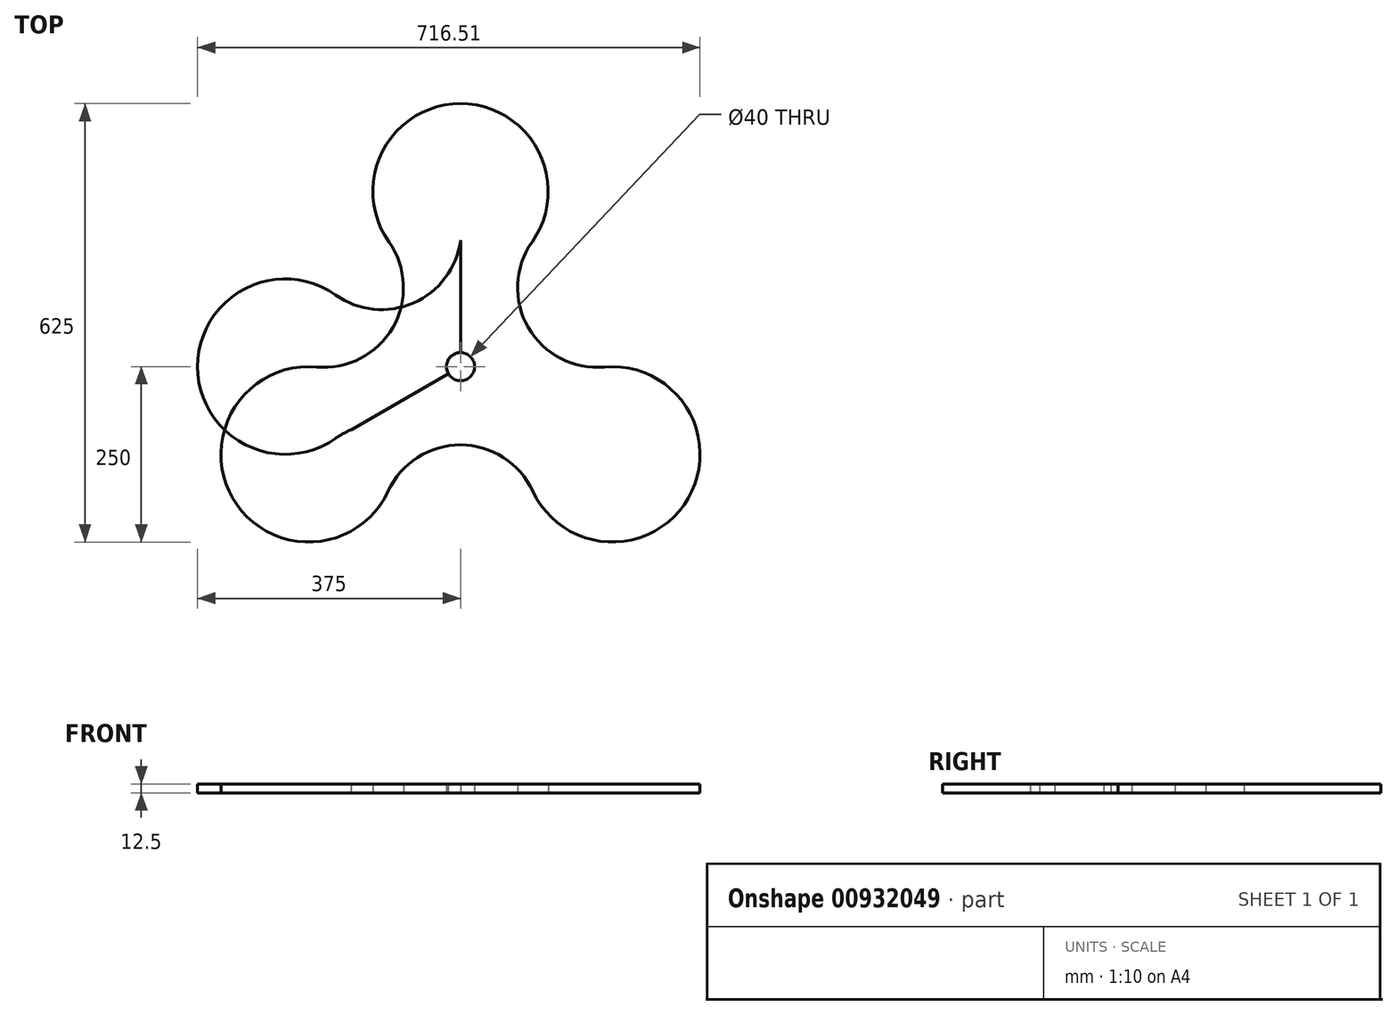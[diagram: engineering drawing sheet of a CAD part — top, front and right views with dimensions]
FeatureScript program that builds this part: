
annotation { "Feature Type Name" : "Feature", "Feature Type Description" : "" }
export const myFeature = defineFeature(function(context is Context, id is Id, definition is map)
    precondition{}
    {
        {
            var Q0;
            Q0=qCreatedBy(makeId("Top.planeOp"),FACE);
            var sketch = newSketch(context, id + "F0", { "sketchPlane" : qUnion([Q0])});
            skCircle(sketch, "E0", {"center": v(0, 0) * mm, "radius": 20 * mm});
            skCircle(sketch, "E1", {"center": v(0, 0) * mm, "radius": 65 * mm, "construction": true});
            skCircle(sketch, "E2", {"center": v(0, 0) * mm, "radius": 100 * mm});
            skLineSegment(sketch, "E3", {"start": v(0, 0) * mm, "end": v(0, 383.92) * mm, "construction": true});
            skCircle(sketch, "E4", {"center": v(0, 0) * mm, "radius": 250 * mm, "construction": true});
            skCircle(sketch, "E5", {"center": v(0, 0) * mm, "radius": 225 * mm, "construction": true});
            skLineSegment(sketch, "E6.1.0", {"start": v(0, 0) * mm, "end": v(-332.48, 191.96) * mm, "construction": true});
            skLineSegment(sketch, "E6.2.0", {"start": v(0, 0) * mm, "end": v(-332.48, -191.96) * mm, "construction": true});
            skLineSegment(sketch, "E6.3.0", {"start": v(0, 0) * mm, "end": v(0, -383.92) * mm, "construction": true});
            skLineSegment(sketch, "E6.4.0", {"start": v(0, 0) * mm, "end": v(332.48, -191.96) * mm, "construction": true});
            skLineSegment(sketch, "E6.5.0", {"start": v(0, 0) * mm, "end": v(332.48, 191.96) * mm, "construction": true});
            skArc(sketch, "E7", {"start": v(102.13, 177.93) * mm, "mid": v(0, 375) * mm, "end": v(-102.13, 177.93) * mm});
            skArc(sketch, "E8", {"start": v(102.13, 177.93) * mm, "mid": v(96.57, 55.76) * mm, "end": v(205.16, -0.52) * mm});
            skArc(sketch, "E9.1.0", {"start": v(-205.16, -0.52) * mm, "mid": v(-324.76, -187.5) * mm, "end": v(-103.03, -177.41) * mm});
            skArc(sketch, "E9.1.1", {"start": v(-205.16, -0.52) * mm, "mid": v(-96.57, 55.76) * mm, "end": v(-102.13, 177.93) * mm});
            skArc(sketch, "E9.2.0", {"start": v(103.03, -177.41) * mm, "mid": v(324.76, -187.5) * mm, "end": v(205.16, -0.52) * mm});
            skArc(sketch, "E9.2.1", {"start": v(103.03, -177.41) * mm, "mid": v(0, -111.52) * mm, "end": v(-103.03, -177.41) * mm});
            skSolve(sketch);
        }
        {
            var Q0;
            Q0=makeQuery(id+"F0.imprint","IMPRINT",FACE,{"disambiguationData":[TD([[makeQuery(id+"F0.imprint","IMPRINT",EDGE,{"derivedFrom":sQuery(id+"F0.wireOp",EDGE,"E2")}),-1.0]])]});
            var Q1;
            Q1=makeQuery(id+"F0.imprint","IMPRINT",FACE,{"disambiguationData":[TD([[makeQuery(id+"F0.imprint","IMPRINT",EDGE,{"derivedFrom":sQuery(id+"F0.wireOp",EDGE,"E0")}),-1.0]])]});
            extrude(context, id + "F1", {"entities" : qUnion([Q0, Q1]), "depth" : 12.5 * mm, "offsetDistance" : 25 * mm});
        }
        {
            var Q0;
            Q0=qCreatedBy(makeId("Top.planeOp"),FACE);
            var sketch = newSketch(context, id + "F2", { "sketchPlane" : qUnion([Q0])});
            skLineSegment(sketch, "E10", {"start": v(0, 0) * mm, "end": v(0, 416.53) * mm, "construction": true});
            skLineSegment(sketch, "E11.1.0", {"start": v(-10, 17.32) * mm, "end": v(-208.27, 360.73) * mm, "construction": true});
            skLineSegment(sketch, "E11.2.0", {"start": v(0, 0) * mm, "end": v(-360.73, 208.27) * mm, "construction": true});
            skLineSegment(sketch, "E11.3.0", {"start": v(0, 0) * mm, "end": v(-416.53, 0) * mm, "construction": true});
            skLineSegment(sketch, "E11.4.0", {"start": v(0, 0) * mm, "end": v(-360.73, -208.27) * mm, "construction": true});
            skLineSegment(sketch, "E11.5.0", {"start": v(0, 0) * mm, "end": v(-208.27, -360.73) * mm, "construction": true});
            skLineSegment(sketch, "E11.6.0", {"start": v(0, 0) * mm, "end": v(0, -416.53) * mm, "construction": true});
            skLineSegment(sketch, "E11.7.0", {"start": v(0, 0) * mm, "end": v(208.27, -360.73) * mm, "construction": true});
            skLineSegment(sketch, "E11.8.0", {"start": v(0, 0) * mm, "end": v(360.73, -208.27) * mm, "construction": true});
            skLineSegment(sketch, "E11.9.0", {"start": v(20, 0) * mm, "end": v(416.53, 0) * mm, "construction": true});
            skLineSegment(sketch, "E11.10.0", {"start": v(0, 0) * mm, "end": v(360.73, 208.27) * mm, "construction": true});
            skLineSegment(sketch, "E11.11.0", {"start": v(0, 0) * mm, "end": v(208.27, 360.73) * mm, "construction": true});
            skPoint(sketch, "E11.center", {"position": v(0, 0) * mm});
            skArc(sketch, "E12.0", {"start": v(102.13, 177.93) * mm, "mid": v(90.88, 67.03) * mm, "end": v(179.94, 0) * mm});
            skArc(sketch, "E13.0", {"start": v(-89.97, 155.83) * mm, "mid": v(-95.43, 167.22) * mm, "end": v(-102.13, 177.93) * mm});
            skLineSegment(sketch, "E14", {"start": v(-10, 17.32) * mm, "end": v(-89.97, 155.83) * mm});
            skLineSegment(sketch, "E15", {"start": v(20, 0) * mm, "end": v(179.94, 0) * mm});
            skArc(sketch, "E16.0", {"start": v(20, 0) * mm, "mid": v(10, 17.32) * mm, "end": v(-10, 17.32) * mm});
            skArc(sketch, "E17.0", {"start": v(102.13, 177.93) * mm, "mid": v(0, 375) * mm, "end": v(-102.13, 177.93) * mm});
            skArc(sketch, "E18.0.0", {"start": v(-102.13, 177.93) * mm, "mid": v(-95.43, 167.22) * mm, "end": v(-89.97, 155.83) * mm});
            skArc(sketch, "E18.0.4", {"start": v(179.94, 0) * mm, "mid": v(90.88, 67.03) * mm, "end": v(102.13, 177.93) * mm});
            skPoint(sketch, "E19.trimOffspring.end.orphan", {"position": v(103.03, -177.41) * mm});
            skPoint(sketch, "E20.trimOffspring.end.orphan", {"position": v(-103.03, -177.41) * mm});
            skPoint(sketch, "E21.orphan", {"position": v(-205.16, -0.52) * mm});
            skPoint(sketch, "E22.trimOffspring.end.orphan", {"position": v(205.16, -0.52) * mm});
            skSolve(sketch);
        }
        {
            var Q0;
            Q0=makeQuery(id+"F2.imprint","IMPRINT",FACE,{"disambiguationData":[TD([[makeQuery(id+"F2.imprint","IMPRINT",EDGE,{"derivedFrom":sQuery(id+"F2.wireOp",EDGE,"E14")}),-1.0]])]});
            extrude(context, id + "F3", {"entities" : qUnion([Q0]), "depth" : 12.5 * mm, "offsetDistance" : 25 * mm});
        }
        {
            var Q0;
            Q0=qCreatedBy(makeId("Front.planeOp"),FACE);
            var sketch = newSketch(context, id + "F4", { "sketchPlane" : qUnion([Q0])});
            skLineSegment(sketch, "E23", {"start": v(0, 0) * mm, "end": v(0, 69.18) * mm});
            skSolve(sketch);
        }
        {
            var Q0;
            Q0=makeQuery(id+"F3.opExtrude","SWEPT_BODY",BODY,{"disambiguationData":[OSD([sQuery(id+"F2.wireOp",EDGE,"E14"),sQuery(id+"F2.wireOp",EDGE,"E15"),sQuery(id+"F2.wireOp",EDGE,"E16.0"),sQuery(id+"F2.wireOp",EDGE,"E18.0.0"),sQuery(id+"F2.wireOp",EDGE,"E18.0.4"),sQuery(id+"F2.wireOp",EDGE,"E17.0")])]});
            var Q1;
            Q1=sQuery(id+"F4.wireOp",EDGE,"E23");
            transform(context, id + "F5", {"entities" : qUnion([Q0]), "transformType" : TransformType.ROTATION, "transformAxis" : qUnion([Q1]), "angle" : 90 * degree, "makeCopy" : false});
        }
    });
